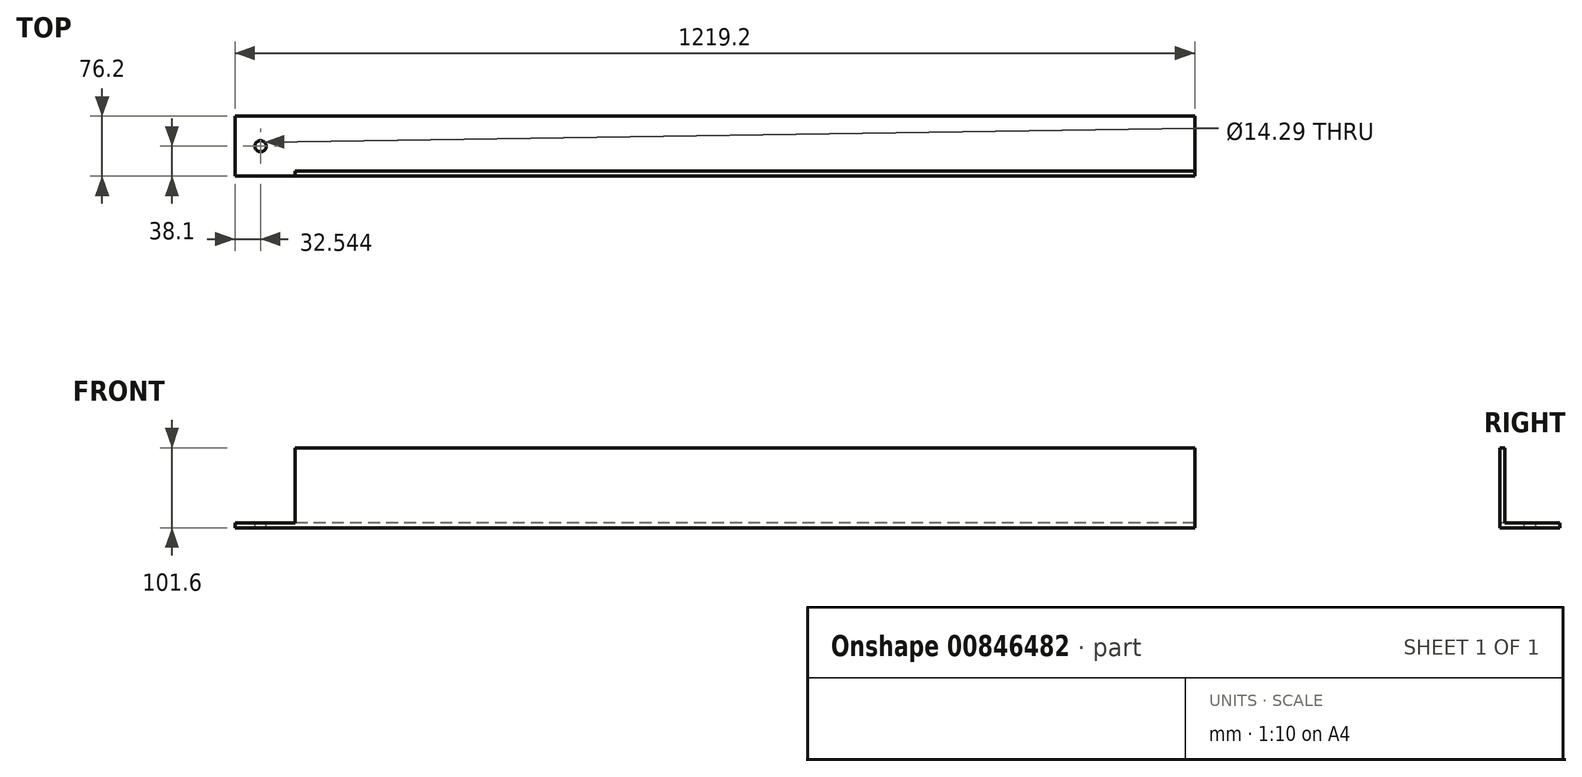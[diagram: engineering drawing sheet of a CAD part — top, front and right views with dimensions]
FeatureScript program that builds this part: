
annotation { "Feature Type Name" : "Feature", "Feature Type Description" : "" }
export const myFeature = defineFeature(function(context is Context, id is Id, definition is map)
    precondition{}
    {
        {
            var Q0;
            Q0=qCreatedBy(makeId("Right.planeOp"),FACE);
            var sketch = newSketch(context, id + "F0", { "sketchPlane" : qUnion([Q0])});
            skLineSegment(sketch, "E0", {"start": v(-6.35, 95.25) * mm, "end": v(-6.35, -6.35) * mm});
            skLineSegment(sketch, "E1", {"start": v(-6.35, -6.35) * mm, "end": v(69.85, -6.35) * mm});
            skLineSegment(sketch, "E2", {"start": v(69.85, -6.35) * mm, "end": v(69.85, 0) * mm});
            skLineSegment(sketch, "E3", {"start": v(69.85, 0) * mm, "end": v(0, 0) * mm});
            skLineSegment(sketch, "E4", {"start": v(0, 0) * mm, "end": v(0, 95.25) * mm});
            skLineSegment(sketch, "E5", {"start": v(0, 95.25) * mm, "end": v(-6.35, 95.25) * mm});
            skSolve(sketch);
        }
        {
            var Q0;
            Q0=qSketchRegion(id+"F0",true);
            extrude(context, id + "F1", {"entities" : qUnion([Q0]), "depth" : 1219.2 * mm, "offsetDistance" : 25.4 * mm});
        }
        {
            var Q0;
            Q0=makeQuery(id+"F1.opExtrude","SWEPT_FACE",FACE,{"disambiguationData":[OSD([sQuery(id+"F0.wireOp",EDGE,"E0")])]});
            var sketch = newSketch(context, id + "F2", { "sketchPlane" : qUnion([Q0])});
            skLineSegment(sketch, "E6.bottom", {"start": v(0, 95.25) * mm, "end": v(76.2, 95.25) * mm});
            skLineSegment(sketch, "E6.top", {"start": v(0, 0) * mm, "end": v(76.2, 0) * mm});
            skLineSegment(sketch, "E6.left", {"start": v(0, 95.25) * mm, "end": v(0, 0) * mm});
            skLineSegment(sketch, "E6.right", {"start": v(76.2, 95.25) * mm, "end": v(76.2, 0) * mm});
            skSolve(sketch);
        }
        {
            var Q0;
            Q0 = qSketchRegion(id + "F2", true);
            extrude(context, id + "F3", {"entities" : qUnion([Q0]), "operationType" : NewBodyOperationType.REMOVE, "oppositeDirection" : true, "depth" : 25.4 * mm, "offsetDistance" : 25.4 * mm});
        }
        {
            var Q0;
            Q0=makeQuery(id+"F3.boolean.opBoolean","MERGE",FACE,{"derivedFrom":[makeQuery(id+"F1.opExtrude","SWEPT_FACE",FACE,{"disambiguationData":[OSD([sQuery(id+"F0.wireOp",EDGE,"E3")])]}),makeQuery(id+"F3.opExtrude","SWEPT_FACE",FACE,{"disambiguationData":[OSD([sQuery(id+"F2.wireOp",EDGE,"E6.top")])]})]});
            var sketch = newSketch(context, id + "F4", { "sketchPlane" : qUnion([Q0])});
            skCircle(sketch, "E7", {"center": v(32.54, 31.75) * mm, "radius": 7.14 * mm});
            skPoint(sketch, "E7.centerSnap0", {"position": v(0, 31.75) * mm});
            skSolve(sketch);
        }
        {
            var Q0;
            Q0 = qSketchRegion(id + "F4", true);
            extrude(context, id + "F5", {"entities" : qUnion([Q0]), "operationType" : NewBodyOperationType.REMOVE, "oppositeDirection" : true, "depth" : 25.4 * mm, "offsetDistance" : 25.4 * mm});
        }
    });
